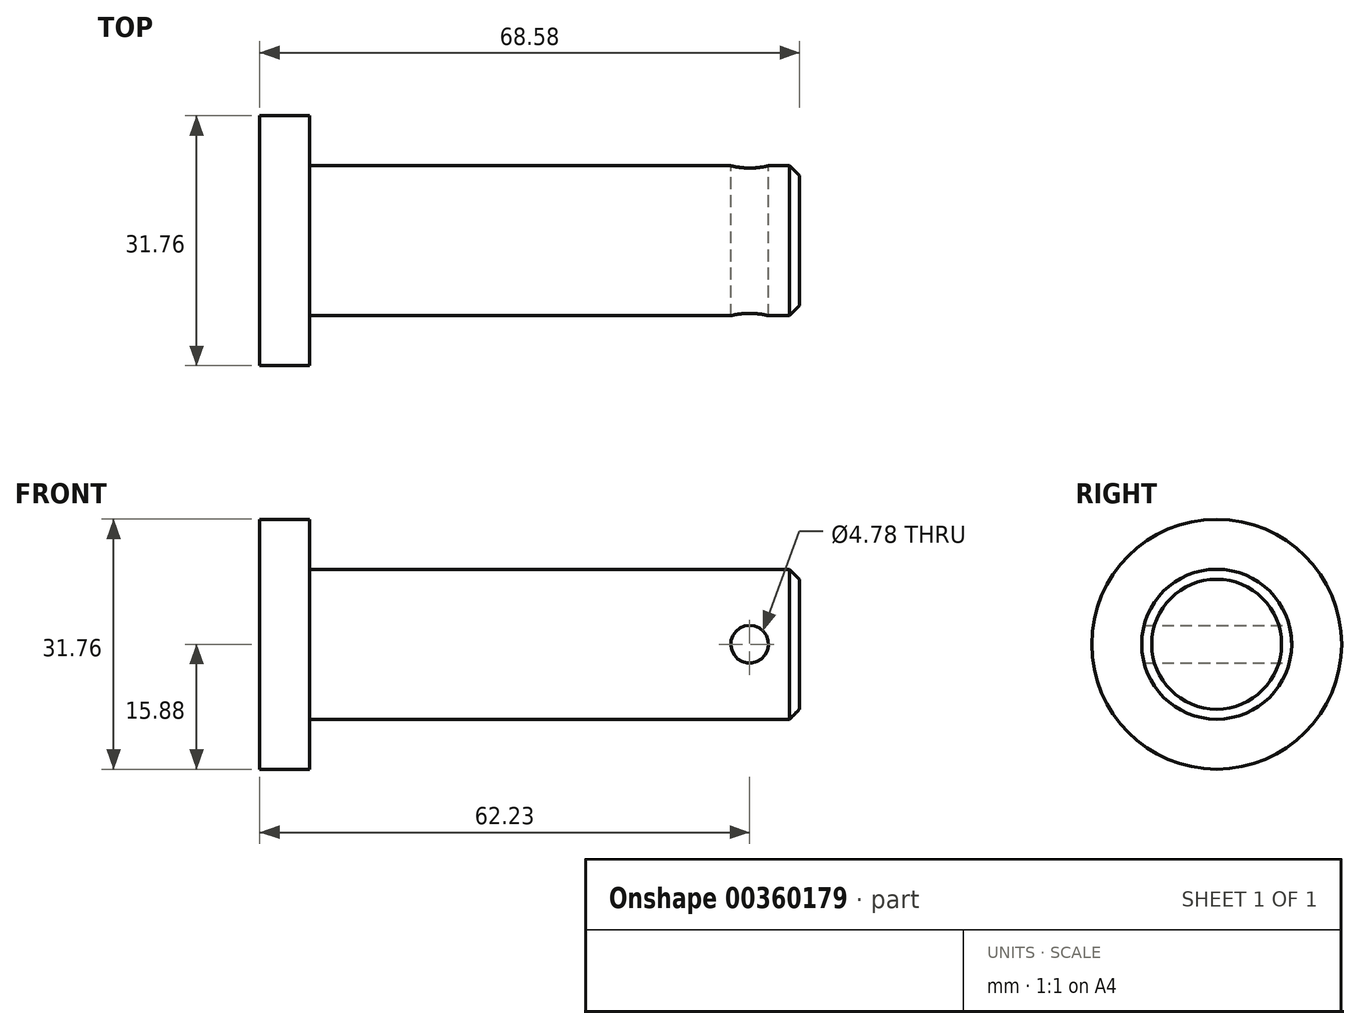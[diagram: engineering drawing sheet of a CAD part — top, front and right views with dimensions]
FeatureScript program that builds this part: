
annotation { "Feature Type Name" : "Feature", "Feature Type Description" : "" }
export const myFeature = defineFeature(function(context is Context, id is Id, definition is map)
    precondition{}
    {
        {
            var Q0;
            Q0=qCreatedBy(makeId("Right.planeOp"),FACE);
            var sketch = newSketch(context, id + "F0", { "sketchPlane" : qUnion([Q0])});
            skCircle(sketch, "E0", {"center": v(0, 0) * mm, "radius": 15.88 * mm});
            skSolve(sketch);
        }
        {
            var Q0;
            Q0=makeQuery(id+"F0.imprint","IMPRINT",FACE,{"disambiguationData":[TD([[makeQuery(id+"F0.imprint","IMPRINT",EDGE,{"derivedFrom":sQuery(id+"F0.wireOp",EDGE,"E0")}),1.0]])]});
            extrude(context, id + "F1", {"entities" : qUnion([Q0]), "depth" : 6.35 * mm});
        }
        {
            var Q0;
            Q0=makeQuery(id+"F1.opExtrude","CAP_FACE",FACE,{"disambiguationData":[OSD([sQuery(id+"F0.wireOp",EDGE,"E0")])],"isStart":false});
            var sketch = newSketch(context, id + "F2", { "sketchPlane" : qUnion([Q0])});
            skCircle(sketch, "E1", {"center": v(0, 0) * mm, "radius": 9.53 * mm});
            skSolve(sketch);
        }
        {
            var Q0;
            Q0=makeQuery(id+"F2.imprint","IMPRINT",FACE,{"disambiguationData":[TD([[makeQuery(id+"F2.imprint","IMPRINT",EDGE,{"derivedFrom":sQuery(id+"F2.wireOp",EDGE,"E1")}),1.0]])]});
            extrude(context, id + "F3", {"entities" : qUnion([Q0]), "operationType" : NewBodyOperationType.ADD, "depth" : 62.23 * mm});
        }
        {
            var Q0;
            Q0=qCreatedBy(makeId("Front.planeOp"),FACE);
            var sketch = newSketch(context, id + "F4", { "sketchPlane" : qUnion([Q0])});
            skCircle(sketch, "E2", {"center": v(62.23, 0) * mm, "radius": 2.39 * mm});
            skSolve(sketch);
        }
        {
            var Q0;
            Q0 = qSketchRegion(id + "F4", true);
            extrude(context, id + "F5", {"entities" : qUnion([Q0]), "operationType" : NewBodyOperationType.REMOVE, "endBound" : BoundingType.SYMMETRIC, "depth" : 25.4 * mm});
        }
        {
            var Q0;
            Q0=makeQuery(id+"F3.opExtrude","CAP_EDGE",EDGE,{"disambiguationData":[OSD([sQuery(id+"F2.wireOp",EDGE,"E1")])],"isStart":false});
            chamfer(context, id + "F6", {"entities" : qUnion([Q0]), "chamferType" : ChamferType.OFFSET_ANGLE, "width" : 1.27 * mm, "oppositeDirection" : false, "angle" : 45 * degree, "tangentPropagation" : true});
        }
    });
